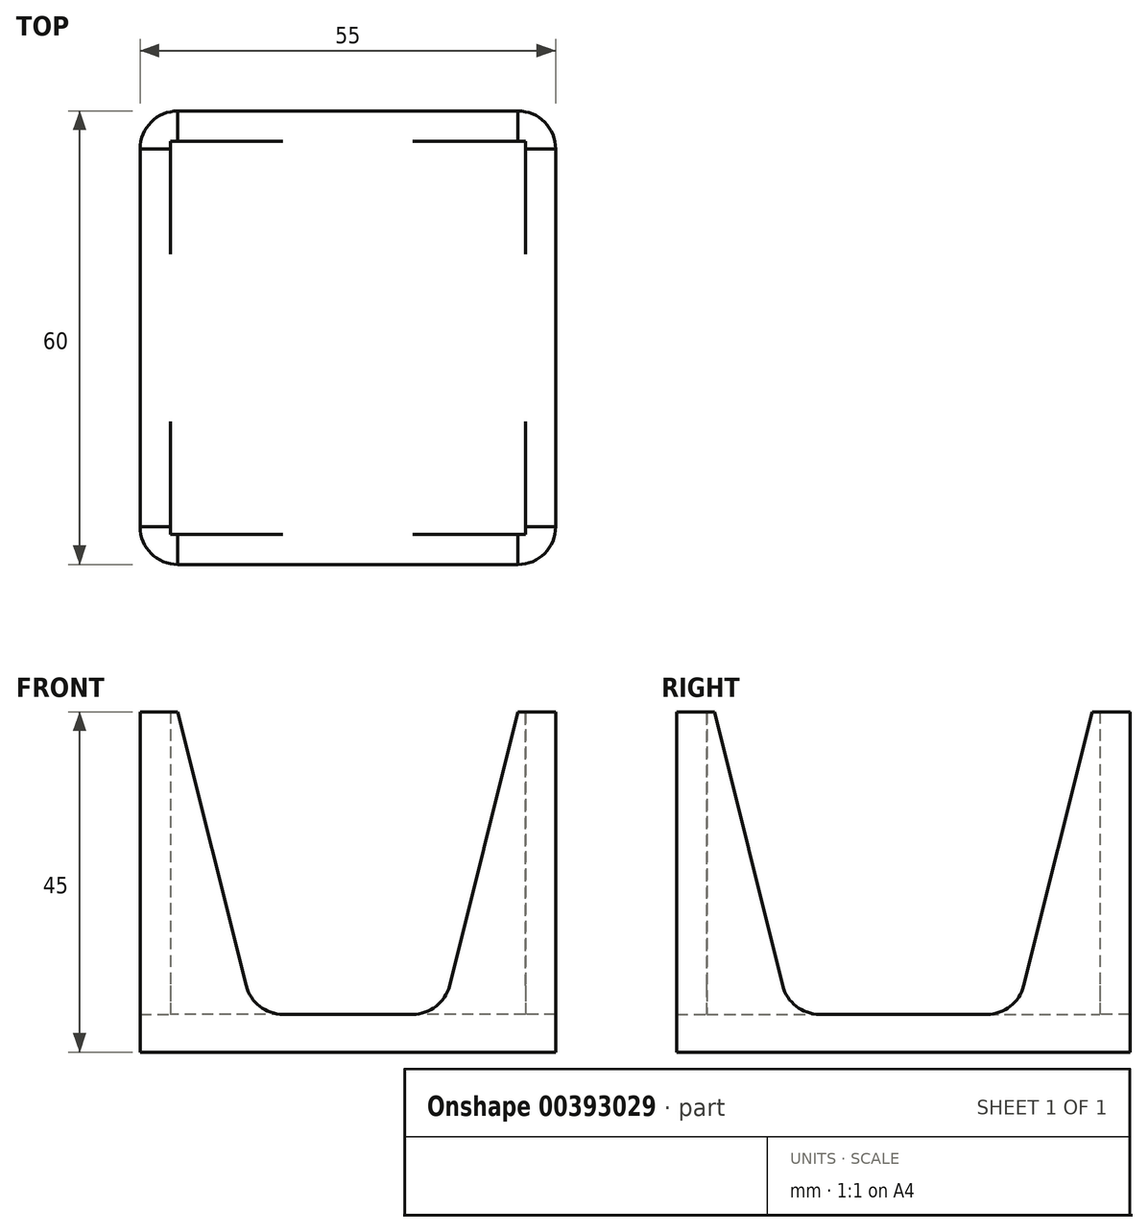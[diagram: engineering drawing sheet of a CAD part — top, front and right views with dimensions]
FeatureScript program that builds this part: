
annotation { "Feature Type Name" : "Feature", "Feature Type Description" : "" }
export const myFeature = defineFeature(function(context is Context, id is Id, definition is map)
    precondition{}
    {
        {
            var Q0;
            Q0=qCreatedBy(makeId("Top.planeOp"),FACE);
            var sketch = newSketch(context, id + "F0", { "sketchPlane" : qUnion([Q0])});
            skLineSegment(sketch, "E0.bottom", {"start": v(-27.5, 30) * mm, "end": v(27.5, 30) * mm});
            skLineSegment(sketch, "E0.top", {"start": v(-27.5, -30) * mm, "end": v(27.5, -30) * mm});
            skLineSegment(sketch, "E0.left", {"start": v(-27.5, 30) * mm, "end": v(-27.5, -30) * mm});
            skLineSegment(sketch, "E0.right", {"start": v(27.5, 30) * mm, "end": v(27.5, -30) * mm});
            skPoint(sketch, "E0.middle", {"position": v(0, 0) * mm});
            skSolve(sketch);
        }
        {
            var Q0;
            Q0=makeQuery(id+"F0.imprint","IMPRINT",FACE,{"disambiguationData":[TD([[makeQuery(id+"F0.imprint","IMPRINT",EDGE,{"derivedFrom":sQuery(id+"F0.wireOp",EDGE,"E0.bottom")}),-1.0]])]});
            extrude(context, id + "F1", {"entities" : qUnion([Q0]), "depth" : 5 * mm});
        }
        {
            var Q0;
            Q0=makeQuery(id+"F1.opExtrude","CAP_FACE",FACE,{"disambiguationData":[OSD([sQuery(id+"F0.wireOp",EDGE,"E0.bottom"),sQuery(id+"F0.wireOp",EDGE,"E0.top"),sQuery(id+"F0.wireOp",EDGE,"E0.left"),sQuery(id+"F0.wireOp",EDGE,"E0.right")])],"isStart":false});
            var sketch = newSketch(context, id + "F2", { "sketchPlane" : qUnion([Q0])});
            skLineSegment(sketch, "E1.0", {"start": v(-23.5, 26) * mm, "end": v(-23.5, -26) * mm});
            skLineSegment(sketch, "E1.1", {"start": v(23.5, 26) * mm, "end": v(-23.5, 26) * mm});
            skLineSegment(sketch, "E1.2", {"start": v(23.5, -26) * mm, "end": v(23.5, 26) * mm});
            skLineSegment(sketch, "E1.3", {"start": v(-23.5, -26) * mm, "end": v(23.5, -26) * mm});
            skLineSegment(sketch, "E2", {"start": v(-27.5, 30) * mm, "end": v(-12.5, 30) * mm, "construction": true});
            skLineSegment(sketch, "E3", {"start": v(-27.5, 30) * mm, "end": v(-27.5, 15) * mm, "construction": true});
            skLineSegment(sketch, "E4", {"start": v(27.5, 30) * mm, "end": v(12.5, 30) * mm, "construction": true});
            skLineSegment(sketch, "E5", {"start": v(-27.5, -30) * mm, "end": v(-27.5, -15) * mm, "construction": true});
            skLineSegment(sketch, "E6", {"start": v(-27.5, 15) * mm, "end": v(27.5, 15) * mm});
            skLineSegment(sketch, "E7", {"start": v(-12.5, 30) * mm, "end": v(-12.5, -30) * mm});
            skLineSegment(sketch, "E8", {"start": v(12.5, 30) * mm, "end": v(12.5, -30) * mm});
            skLineSegment(sketch, "E9", {"start": v(-27.5, -15) * mm, "end": v(27.5, -15) * mm});
            skSolve(sketch);
        }
        {
            var Q0;
            {var subQ3=sQuery(id+"F2.wireOp",EDGE,"E1.1");var subQ8=sQuery(id+"F2.wireOp",EDGE,"E1.0");var subQ10=makeQuery(id+"F2.imprint","INTERSECT",VERTEX,{"derivedFrom":[subQ8,subQ3]});Q0=makeQuery(id+"F2.imprint","IMPRINT",FACE,{"disambiguationData":[TD([[makeQuery(id+"F2.imprint","IMPRINT",EDGE,{"disambiguationData":[TD([[subQ10,-1.0]])],"derivedFrom":subQ8}),-1.0]])]});}
            var Q1;
            {var subQ3=sQuery(id+"F2.wireOp",EDGE,"E1.1");var subQ9=sQuery(id+"F2.wireOp",EDGE,"E1.2");var subQ11=makeQuery(id+"F2.imprint","INTERSECT",VERTEX,{"derivedFrom":[subQ3,subQ9]});Q1=makeQuery(id+"F2.imprint","IMPRINT",FACE,{"disambiguationData":[TD([[makeQuery(id+"F2.imprint","IMPRINT",EDGE,{"disambiguationData":[TD([[subQ11,-1.0]])],"derivedFrom":subQ3}),-1.0]])]});}
            var Q2;
            {var subQ3=sQuery(id+"F2.wireOp",EDGE,"E1.2");var subQ9=sQuery(id+"F2.wireOp",EDGE,"E1.3");var subQ11=makeQuery(id+"F2.imprint","INTERSECT",VERTEX,{"derivedFrom":[subQ3,subQ9]});Q2=makeQuery(id+"F2.imprint","IMPRINT",FACE,{"disambiguationData":[TD([[makeQuery(id+"F2.imprint","IMPRINT",EDGE,{"disambiguationData":[TD([[subQ11,-1.0]])],"derivedFrom":subQ3}),-1.0]])]});}
            var Q3;
            {var subQ3=sQuery(id+"F2.wireOp",EDGE,"E1.3");var subQ5=sQuery(id+"F2.wireOp",EDGE,"E1.0");var subQ6=makeQuery(id+"F2.imprint","INTERSECT",VERTEX,{"derivedFrom":[subQ5,subQ3]});Q3=makeQuery(id+"F2.imprint","IMPRINT",FACE,{"disambiguationData":[TD([[makeQuery(id+"F2.imprint","IMPRINT",EDGE,{"disambiguationData":[TD([[subQ6,1.0]])],"derivedFrom":subQ5}),-1.0]])]});}
            extrude(context, id + "F3", {"entities" : qUnion([Q0, Q1, Q2, Q3]), "operationType" : NewBodyOperationType.ADD, "depth" : 40 * mm});
        }
        {
            var Q0;
            {var subQ0=sQuery(id+"F2.wireOp",EDGE,"E9");Q0=makeQuery(id+"F3.opExtrude","CAP_EDGE",EDGE,{"disambiguationData":[OSD([subQ0]),TDD([makeQuery(id+"F2.imprint","IMPRINT",EDGE,{"disambiguationData":[TD([[makeQuery(id+"F2.imprint","INTERSECT",VERTEX,{"derivedFrom":[makeQuery(id+"F1.opExtrude","CAP_EDGE",EDGE,{"disambiguationData":[OSD([sQuery(id+"F0.wireOp",EDGE,"E0.left")])],"isStart":false}),subQ0]}),-1.0]])],"derivedFrom":subQ0})])],"isStart":false});}
            var Q1;
            {var subQ0=sQuery(id+"F2.wireOp",EDGE,"E9");Q1=makeQuery(id+"F3.opExtrude","CAP_EDGE",EDGE,{"disambiguationData":[OSD([subQ0]),TDD([makeQuery(id+"F2.imprint","IMPRINT",EDGE,{"disambiguationData":[TD([[makeQuery(id+"F2.imprint","INTERSECT",VERTEX,{"derivedFrom":[makeQuery(id+"F1.opExtrude","CAP_EDGE",EDGE,{"disambiguationData":[OSD([sQuery(id+"F0.wireOp",EDGE,"E0.right")])],"isStart":false}),subQ0]}),1.0]])],"derivedFrom":subQ0})])],"isStart":false});}
            var Q2;
            {var subQ0=sQuery(id+"F2.wireOp",EDGE,"E7");Q2=makeQuery(id+"F3.opExtrude","CAP_EDGE",EDGE,{"disambiguationData":[OSD([subQ0]),TDD([makeQuery(id+"F2.imprint","IMPRINT",EDGE,{"disambiguationData":[TD([[makeQuery(id+"F2.imprint","INTERSECT",VERTEX,{"derivedFrom":[makeQuery(id+"F1.opExtrude","CAP_EDGE",EDGE,{"disambiguationData":[OSD([sQuery(id+"F0.wireOp",EDGE,"E0.bottom")])],"isStart":false}),subQ0]}),-1.0]])],"derivedFrom":subQ0})])],"isStart":false});}
            chamfer(context, id + "F4", {"entities" : qUnion([Q0, Q1, Q2]), "chamferType" : ChamferType.TWO_OFFSETS, "width1" : 40 * mm, "oppositeDirection" : false, "width2" : 10 * mm, "tangentPropagation" : true});
        }
        {
            var Q0;
            {var subQ0=sQuery(id+"F2.wireOp",EDGE,"E6");Q0=makeQuery(id+"F3.opExtrude","CAP_EDGE",EDGE,{"disambiguationData":[OSD([subQ0]),TDD([makeQuery(id+"F2.imprint","IMPRINT",EDGE,{"disambiguationData":[TD([[makeQuery(id+"F2.imprint","INTERSECT",VERTEX,{"derivedFrom":[makeQuery(id+"F1.opExtrude","CAP_EDGE",EDGE,{"disambiguationData":[OSD([sQuery(id+"F0.wireOp",EDGE,"E0.left")])],"isStart":false}),subQ0]}),-1.0]])],"derivedFrom":subQ0})])],"isStart":false});}
            var Q1;
            {var subQ0=sQuery(id+"F2.wireOp",EDGE,"E8");Q1=makeQuery(id+"F3.opExtrude","CAP_EDGE",EDGE,{"disambiguationData":[OSD([subQ0]),TDD([makeQuery(id+"F2.imprint","IMPRINT",EDGE,{"disambiguationData":[TD([[makeQuery(id+"F2.imprint","INTERSECT",VERTEX,{"derivedFrom":[makeQuery(id+"F1.opExtrude","CAP_EDGE",EDGE,{"disambiguationData":[OSD([sQuery(id+"F0.wireOp",EDGE,"E0.top")])],"isStart":false}),subQ0]}),1.0]])],"derivedFrom":subQ0})])],"isStart":false});}
            var Q2;
            {var subQ0=sQuery(id+"F2.wireOp",EDGE,"E6");Q2=makeQuery(id+"F3.opExtrude","CAP_EDGE",EDGE,{"disambiguationData":[OSD([subQ0]),TDD([makeQuery(id+"F2.imprint","IMPRINT",EDGE,{"disambiguationData":[TD([[makeQuery(id+"F2.imprint","INTERSECT",VERTEX,{"derivedFrom":[makeQuery(id+"F1.opExtrude","CAP_EDGE",EDGE,{"disambiguationData":[OSD([sQuery(id+"F0.wireOp",EDGE,"E0.right")])],"isStart":false}),subQ0]}),1.0]])],"derivedFrom":subQ0})])],"isStart":false});}
            var Q3;
            {var subQ0=sQuery(id+"F2.wireOp",EDGE,"E8");Q3=makeQuery(id+"F3.opExtrude","CAP_EDGE",EDGE,{"disambiguationData":[OSD([subQ0]),TDD([makeQuery(id+"F2.imprint","IMPRINT",EDGE,{"disambiguationData":[TD([[makeQuery(id+"F2.imprint","INTERSECT",VERTEX,{"derivedFrom":[makeQuery(id+"F1.opExtrude","CAP_EDGE",EDGE,{"disambiguationData":[OSD([sQuery(id+"F0.wireOp",EDGE,"E0.bottom")])],"isStart":false}),subQ0]}),-1.0]])],"derivedFrom":subQ0})])],"isStart":false});}
            chamfer(context, id + "F5", {"entities" : qUnion([Q0, Q1, Q2, Q3]), "chamferType" : ChamferType.TWO_OFFSETS, "width1" : 10 * mm, "oppositeDirection" : false, "width2" : 40 * mm, "tangentPropagation" : true});
        }
        {
            var Q0;
            {var subQ0=sQuery(id+"F2.wireOp",EDGE,"E7");Q0=makeQuery(id+"F3.opExtrude","CAP_EDGE",EDGE,{"disambiguationData":[OSD([subQ0]),TDD([makeQuery(id+"F2.imprint","IMPRINT",EDGE,{"disambiguationData":[TD([[makeQuery(id+"F2.imprint","INTERSECT",VERTEX,{"derivedFrom":[makeQuery(id+"F1.opExtrude","CAP_EDGE",EDGE,{"disambiguationData":[OSD([sQuery(id+"F0.wireOp",EDGE,"E0.top")])],"isStart":false}),subQ0]}),1.0]])],"derivedFrom":subQ0})])],"isStart":false});}
            chamfer(context, id + "F6", {"entities" : qUnion([Q0]), "chamferType" : ChamferType.TWO_OFFSETS, "width1" : 40 * mm, "oppositeDirection" : false, "width2" : 10 * mm, "tangentPropagation" : true});
        }
        {
            var Q0;
            {var subQ0=sQuery(id+"F0.wireOp",EDGE,"E0.left");var subQ1=sQuery(id+"F0.wireOp",EDGE,"E0.top");Q0=makeQuery(id+"F3.boolean.opBoolean","MERGE",EDGE,{"derivedFrom":[makeQuery(id+"F1.opExtrude","SWEPT_EDGE",EDGE,{"disambiguationData":[OSD([subQ1,subQ0])]}),makeQuery(id+"F3.opExtrude","SWEPT_EDGE",EDGE,{"disambiguationData":[OSD([subQ1,subQ0])]})]});}
            var Q1;
            {var subQ0=sQuery(id+"F0.wireOp",EDGE,"E0.right");var subQ1=sQuery(id+"F0.wireOp",EDGE,"E0.top");Q1=makeQuery(id+"F3.boolean.opBoolean","MERGE",EDGE,{"derivedFrom":[makeQuery(id+"F1.opExtrude","SWEPT_EDGE",EDGE,{"disambiguationData":[OSD([subQ1,subQ0])]}),makeQuery(id+"F3.opExtrude","SWEPT_EDGE",EDGE,{"disambiguationData":[OSD([subQ1,subQ0])]})]});}
            var Q2;
            {var subQ0=sQuery(id+"F0.wireOp",EDGE,"E0.right");var subQ1=sQuery(id+"F0.wireOp",EDGE,"E0.bottom");Q2=makeQuery(id+"F3.boolean.opBoolean","MERGE",EDGE,{"derivedFrom":[makeQuery(id+"F1.opExtrude","SWEPT_EDGE",EDGE,{"disambiguationData":[OSD([subQ1,subQ0])]}),makeQuery(id+"F3.opExtrude","SWEPT_EDGE",EDGE,{"disambiguationData":[OSD([subQ1,subQ0])]})]});}
            var Q3;
            {var subQ0=sQuery(id+"F0.wireOp",EDGE,"E0.left");var subQ1=sQuery(id+"F0.wireOp",EDGE,"E0.bottom");Q3=makeQuery(id+"F3.boolean.opBoolean","MERGE",EDGE,{"derivedFrom":[makeQuery(id+"F1.opExtrude","SWEPT_EDGE",EDGE,{"disambiguationData":[OSD([subQ1,subQ0])]}),makeQuery(id+"F3.opExtrude","SWEPT_EDGE",EDGE,{"disambiguationData":[OSD([subQ1,subQ0])]})]});}
            fillet(context, id + "F7", {"entities" : qUnion([Q0, Q1, Q2, Q3]), "radius" : 5 * mm, "tangentPropagation" : true, "allowEdgeOverflow" : false});
        }
        {
            var Q0;
            {var subQ0=sQuery(id+"F0.wireOp",EDGE,"E0.top");var subQ1=sQuery(id+"F2.wireOp",EDGE,"E8");Q0=makeQuery(id+"F5.opChamfer","BLEND_EDGE",EDGE,{"blendedFrom":[makeQuery(id+"F3.opExtrude","CAP_EDGE",EDGE,{"disambiguationData":[OSD([subQ1]),TDD([makeQuery(id+"F2.imprint","IMPRINT",EDGE,{"disambiguationData":[TD([[makeQuery(id+"F2.imprint","INTERSECT",VERTEX,{"derivedFrom":[makeQuery(id+"F1.opExtrude","CAP_EDGE",EDGE,{"disambiguationData":[OSD([subQ0])],"isStart":false}),subQ1]}),1.0]])],"derivedFrom":subQ1})])],"isStart":false}),makeQuery(id+"F1.opExtrude","CAP_FACE",FACE,{"disambiguationData":[OSD([sQuery(id+"F0.wireOp",EDGE,"E0.bottom"),subQ0,sQuery(id+"F0.wireOp",EDGE,"E0.left"),sQuery(id+"F0.wireOp",EDGE,"E0.right")])],"isStart":false})],"blendedInto":[makeQuery(id+"F1.opExtrude","CAP_FACE",FACE,{"disambiguationData":[OSD([sQuery(id+"F0.wireOp",EDGE,"E0.bottom"),subQ0,sQuery(id+"F0.wireOp",EDGE,"E0.left"),sQuery(id+"F0.wireOp",EDGE,"E0.right")])],"isStart":false})]});}
            var Q1;
            {var subQ0=sQuery(id+"F0.wireOp",EDGE,"E0.bottom");var subQ1=sQuery(id+"F2.wireOp",EDGE,"E8");Q1=makeQuery(id+"F5.opChamfer","BLEND_EDGE",EDGE,{"blendedFrom":[makeQuery(id+"F3.opExtrude","CAP_EDGE",EDGE,{"disambiguationData":[OSD([subQ1]),TDD([makeQuery(id+"F2.imprint","IMPRINT",EDGE,{"disambiguationData":[TD([[makeQuery(id+"F2.imprint","INTERSECT",VERTEX,{"derivedFrom":[makeQuery(id+"F1.opExtrude","CAP_EDGE",EDGE,{"disambiguationData":[OSD([subQ0])],"isStart":false}),subQ1]}),-1.0]])],"derivedFrom":subQ1})])],"isStart":false}),makeQuery(id+"F1.opExtrude","CAP_FACE",FACE,{"disambiguationData":[OSD([subQ0,sQuery(id+"F0.wireOp",EDGE,"E0.top"),sQuery(id+"F0.wireOp",EDGE,"E0.left"),sQuery(id+"F0.wireOp",EDGE,"E0.right")])],"isStart":false})],"blendedInto":[makeQuery(id+"F1.opExtrude","CAP_FACE",FACE,{"disambiguationData":[OSD([subQ0,sQuery(id+"F0.wireOp",EDGE,"E0.top"),sQuery(id+"F0.wireOp",EDGE,"E0.left"),sQuery(id+"F0.wireOp",EDGE,"E0.right")])],"isStart":false})]});}
            var Q2;
            {var subQ0=sQuery(id+"F0.wireOp",EDGE,"E0.right");var subQ1=sQuery(id+"F2.wireOp",EDGE,"E6");Q2=makeQuery(id+"F5.opChamfer","BLEND_EDGE",EDGE,{"blendedFrom":[makeQuery(id+"F3.opExtrude","CAP_EDGE",EDGE,{"disambiguationData":[OSD([subQ1]),TDD([makeQuery(id+"F2.imprint","IMPRINT",EDGE,{"disambiguationData":[TD([[makeQuery(id+"F2.imprint","INTERSECT",VERTEX,{"derivedFrom":[makeQuery(id+"F1.opExtrude","CAP_EDGE",EDGE,{"disambiguationData":[OSD([subQ0])],"isStart":false}),subQ1]}),1.0]])],"derivedFrom":subQ1})])],"isStart":false}),makeQuery(id+"F1.opExtrude","CAP_FACE",FACE,{"disambiguationData":[OSD([sQuery(id+"F0.wireOp",EDGE,"E0.bottom"),sQuery(id+"F0.wireOp",EDGE,"E0.top"),sQuery(id+"F0.wireOp",EDGE,"E0.left"),subQ0])],"isStart":false})],"blendedInto":[makeQuery(id+"F1.opExtrude","CAP_FACE",FACE,{"disambiguationData":[OSD([sQuery(id+"F0.wireOp",EDGE,"E0.bottom"),sQuery(id+"F0.wireOp",EDGE,"E0.top"),sQuery(id+"F0.wireOp",EDGE,"E0.left"),subQ0])],"isStart":false})]});}
            var Q3;
            {var subQ0=sQuery(id+"F0.wireOp",EDGE,"E0.left");var subQ1=sQuery(id+"F2.wireOp",EDGE,"E6");Q3=makeQuery(id+"F5.opChamfer","BLEND_EDGE",EDGE,{"blendedFrom":[makeQuery(id+"F3.opExtrude","CAP_EDGE",EDGE,{"disambiguationData":[OSD([subQ1]),TDD([makeQuery(id+"F2.imprint","IMPRINT",EDGE,{"disambiguationData":[TD([[makeQuery(id+"F2.imprint","INTERSECT",VERTEX,{"derivedFrom":[makeQuery(id+"F1.opExtrude","CAP_EDGE",EDGE,{"disambiguationData":[OSD([subQ0])],"isStart":false}),subQ1]}),-1.0]])],"derivedFrom":subQ1})])],"isStart":false}),makeQuery(id+"F1.opExtrude","CAP_FACE",FACE,{"disambiguationData":[OSD([sQuery(id+"F0.wireOp",EDGE,"E0.bottom"),sQuery(id+"F0.wireOp",EDGE,"E0.top"),subQ0,sQuery(id+"F0.wireOp",EDGE,"E0.right")])],"isStart":false})],"blendedInto":[makeQuery(id+"F1.opExtrude","CAP_FACE",FACE,{"disambiguationData":[OSD([sQuery(id+"F0.wireOp",EDGE,"E0.bottom"),sQuery(id+"F0.wireOp",EDGE,"E0.top"),subQ0,sQuery(id+"F0.wireOp",EDGE,"E0.right")])],"isStart":false})]});}
            var Q4;
            {var subQ0=sQuery(id+"F0.wireOp",EDGE,"E0.bottom");var subQ1=sQuery(id+"F2.wireOp",EDGE,"E7");Q4=makeQuery(id+"F4.opChamfer","BLEND_EDGE",EDGE,{"blendedFrom":[makeQuery(id+"F3.opExtrude","CAP_EDGE",EDGE,{"disambiguationData":[OSD([subQ1]),TDD([makeQuery(id+"F2.imprint","IMPRINT",EDGE,{"disambiguationData":[TD([[makeQuery(id+"F2.imprint","INTERSECT",VERTEX,{"derivedFrom":[makeQuery(id+"F1.opExtrude","CAP_EDGE",EDGE,{"disambiguationData":[OSD([subQ0])],"isStart":false}),subQ1]}),-1.0]])],"derivedFrom":subQ1})])],"isStart":false}),makeQuery(id+"F1.opExtrude","CAP_FACE",FACE,{"disambiguationData":[OSD([subQ0,sQuery(id+"F0.wireOp",EDGE,"E0.top"),sQuery(id+"F0.wireOp",EDGE,"E0.left"),sQuery(id+"F0.wireOp",EDGE,"E0.right")])],"isStart":false})],"blendedInto":[makeQuery(id+"F1.opExtrude","CAP_FACE",FACE,{"disambiguationData":[OSD([subQ0,sQuery(id+"F0.wireOp",EDGE,"E0.top"),sQuery(id+"F0.wireOp",EDGE,"E0.left"),sQuery(id+"F0.wireOp",EDGE,"E0.right")])],"isStart":false})]});}
            var Q5;
            {var subQ0=sQuery(id+"F0.wireOp",EDGE,"E0.left");var subQ1=sQuery(id+"F2.wireOp",EDGE,"E9");Q5=makeQuery(id+"F4.opChamfer","BLEND_EDGE",EDGE,{"blendedFrom":[makeQuery(id+"F3.opExtrude","CAP_EDGE",EDGE,{"disambiguationData":[OSD([subQ1]),TDD([makeQuery(id+"F2.imprint","IMPRINT",EDGE,{"disambiguationData":[TD([[makeQuery(id+"F2.imprint","INTERSECT",VERTEX,{"derivedFrom":[makeQuery(id+"F1.opExtrude","CAP_EDGE",EDGE,{"disambiguationData":[OSD([subQ0])],"isStart":false}),subQ1]}),-1.0]])],"derivedFrom":subQ1})])],"isStart":false}),makeQuery(id+"F1.opExtrude","CAP_FACE",FACE,{"disambiguationData":[OSD([sQuery(id+"F0.wireOp",EDGE,"E0.bottom"),sQuery(id+"F0.wireOp",EDGE,"E0.top"),subQ0,sQuery(id+"F0.wireOp",EDGE,"E0.right")])],"isStart":false})],"blendedInto":[makeQuery(id+"F1.opExtrude","CAP_FACE",FACE,{"disambiguationData":[OSD([sQuery(id+"F0.wireOp",EDGE,"E0.bottom"),sQuery(id+"F0.wireOp",EDGE,"E0.top"),subQ0,sQuery(id+"F0.wireOp",EDGE,"E0.right")])],"isStart":false})]});}
            var Q6;
            {var subQ0=sQuery(id+"F0.wireOp",EDGE,"E0.top");var subQ1=sQuery(id+"F2.wireOp",EDGE,"E7");Q6=makeQuery(id+"F6.opChamfer","BLEND_EDGE",EDGE,{"blendedFrom":[makeQuery(id+"F3.opExtrude","CAP_EDGE",EDGE,{"disambiguationData":[OSD([subQ1]),TDD([makeQuery(id+"F2.imprint","IMPRINT",EDGE,{"disambiguationData":[TD([[makeQuery(id+"F2.imprint","INTERSECT",VERTEX,{"derivedFrom":[makeQuery(id+"F1.opExtrude","CAP_EDGE",EDGE,{"disambiguationData":[OSD([subQ0])],"isStart":false}),subQ1]}),1.0]])],"derivedFrom":subQ1})])],"isStart":false}),makeQuery(id+"F1.opExtrude","CAP_FACE",FACE,{"disambiguationData":[OSD([sQuery(id+"F0.wireOp",EDGE,"E0.bottom"),subQ0,sQuery(id+"F0.wireOp",EDGE,"E0.left"),sQuery(id+"F0.wireOp",EDGE,"E0.right")])],"isStart":false})],"blendedInto":[makeQuery(id+"F1.opExtrude","CAP_FACE",FACE,{"disambiguationData":[OSD([sQuery(id+"F0.wireOp",EDGE,"E0.bottom"),subQ0,sQuery(id+"F0.wireOp",EDGE,"E0.left"),sQuery(id+"F0.wireOp",EDGE,"E0.right")])],"isStart":false})]});}
            var Q7;
            {var subQ0=sQuery(id+"F0.wireOp",EDGE,"E0.right");var subQ1=sQuery(id+"F2.wireOp",EDGE,"E9");Q7=makeQuery(id+"F4.opChamfer","BLEND_EDGE",EDGE,{"blendedFrom":[makeQuery(id+"F3.opExtrude","CAP_EDGE",EDGE,{"disambiguationData":[OSD([subQ1]),TDD([makeQuery(id+"F2.imprint","IMPRINT",EDGE,{"disambiguationData":[TD([[makeQuery(id+"F2.imprint","INTERSECT",VERTEX,{"derivedFrom":[makeQuery(id+"F1.opExtrude","CAP_EDGE",EDGE,{"disambiguationData":[OSD([subQ0])],"isStart":false}),subQ1]}),1.0]])],"derivedFrom":subQ1})])],"isStart":false}),makeQuery(id+"F1.opExtrude","CAP_FACE",FACE,{"disambiguationData":[OSD([sQuery(id+"F0.wireOp",EDGE,"E0.bottom"),sQuery(id+"F0.wireOp",EDGE,"E0.top"),sQuery(id+"F0.wireOp",EDGE,"E0.left"),subQ0])],"isStart":false})],"blendedInto":[makeQuery(id+"F1.opExtrude","CAP_FACE",FACE,{"disambiguationData":[OSD([sQuery(id+"F0.wireOp",EDGE,"E0.bottom"),sQuery(id+"F0.wireOp",EDGE,"E0.top"),sQuery(id+"F0.wireOp",EDGE,"E0.left"),subQ0])],"isStart":false})]});}
            fillet(context, id + "F8", {"entities" : qUnion([Q0, Q1, Q2, Q3, Q4, Q5, Q6, Q7]), "radius" : 5 * mm, "tangentPropagation" : true, "allowEdgeOverflow" : false});
        }
    });
